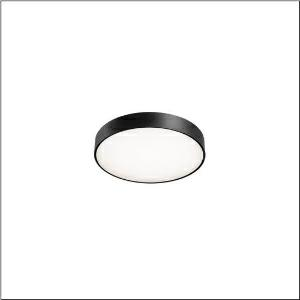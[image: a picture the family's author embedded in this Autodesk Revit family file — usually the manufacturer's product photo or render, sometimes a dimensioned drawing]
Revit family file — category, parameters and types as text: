
# Revit family: round_21_s_51mr34gd0421b
name_source: partatom
category: Lighting Fixtures
units: mm (PartAtom-declared; Revit-internal decimal feet)

## family parameters
Cut with Voids When Loaded = No
Host = Face
Light Source = No
Part Type = Normal
Room Calculation Point = No
Round Connector Dimension = Use Diameter
Shared = No

## types (1)
- Round 21 S (1 x LED, 4090 lm, 28.3 W, 4000K)
    Apparent Load = 28 VA
    CIE Flux Codes = 49 80 96 79 100
    Color Rendering = 80
    Color Temperature = 4000K
    Default Elevation = 1800 mm
    Description = Round 21 S, wall and ceiling luminaire, primary optical cover: cover, of PMMA, opal, light emission: direct/indirect distribution, primary light characteristic: symmetric, installation type: suspended mounting, surface-mounted, LED, rated luminous flux: 4.090lm, luminous efficacy: 135lm/W, light colour: 840, colour temperature: 4000K, control gear: DALI 2, with terminal, 5-pole, mains connection: 230V, AC, 50/60Hz, rated input power: 28.3W, housing, of aluminium, coated, black, diameter: 400mm, height: 62mm, protection rating (complete): IP40, insulation class (complete): insulation class I (protective earthing), certification: CE, impact resistance: IK04, permissible operating ambient temperature: -10..+35°C, packaging unit: 1 piece
    Height = 87 mm
    Lamp = 1 x LED
    Lamp Light Flux = 4090 lm
    Lamp Power = 28.3 W
    Lamp count = 1
    Length = 400 mm
    Luminous efficacy = 145 lm/W
    Manufacturer = Siteco
    ModVariant = No
    Model = 51MR34GD0421B
    Mounting Place = Ceiling
    Mounting Type = Surface mounted
    Number of Poles = 1
    OnlyDefault = Yes
    Power Factor = 1
    Product Name = Round 21 S
    Product group = wall and ceiling luminaire | ceiling mounted
    ProductGroupID = 304
    Protection Class = Protection class I
    Protection Degree = IP 40
    RLX_Detail_Level = 1
    RLX_Emergency_Light_Flux = 0 lm
    RLX_Emergency_Type = 0
    RLX_Emergency_Type_DB = No
    RlxData = <blob elided: 13885 chars, md5=e2e305d9>
    Socket = socket
    Standby Power = 0 W
    System Light Flux = 4090 lm
    System Power = 28 W
    Type Comments = Product without accessories
    Type Image = l_1258311.jpg
    URL = http://relux.com
    VarID = ---
    Voltage = 0 V
    Weight = 0.00 kg
    Width = 0 mm  [stored 0 ft]

note: [stored X ft] marks values corroborated as IEEE doubles in the binary element streams (Revit-internal decimal feet)

## geometry (parser evidence)
native form markers: Sweep x14
no freeform markers — native parametric forms only
